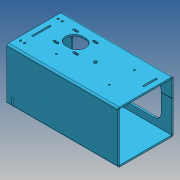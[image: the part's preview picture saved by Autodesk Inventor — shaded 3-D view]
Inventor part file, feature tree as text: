
AUTODESK INVENTOR PART (.ipt)
format: ipt  version: 2017 (Build 210142000, 142)  size: 420,352 bytes
history: native  units: mm
features: other x15, sketch x5, extrude x3, projected_geometry x1
ambient origin geometry x8: Origin, YZ Plane, XZ Plane, XY Plane, X Axis, Y Axis, Z Axis, Center Point
bodies: Body1 (feature_tree)
feature tree (24):
  other  "Sólido1"
  extrude  "Extrusión1"  Depth=56.4mm
  other  "Pestaña1"
  sketch  "Boceto4"  dims[d7=11.235mm]
  other  "Cara1"
  other  "Cara2"
  sketch  "Boceto5"  dims[d8=5.0mm d9=39.14mm d10=8.0mm d11=55.14mm d12=8.0mm d13=4.0mm d14=115.0mm d15=25.0mm d16=60.0mm d17=60.0mm d18=4.0mm d19=20.0mm d20=22.0mm d21=128.27mm d22=50.0mm d23=25.0mm d24=4.0mm d25=0.0mm d26=4.0mm d27=2.0mm d28=8.0mm d29=4.0mm d30=120.0mm d31=90.0deg d32=0.1mm d33=16.0mm d34=4.0mm d35=4.0mm d36=4.0mm d37=8.0mm d38=25.0mm d39=25.0mm d40=4.0mm d41=0.0mm d42=47.14mm d43=47.14mm d44=20.0mm d45=8.0mm d46=8.0mm d47=15.0mm d48=0.1mm d49=4.0mm d50=2.0mm d51=8.0mm d52=4.0mm d53=0.1mm d54=4.0mm d55=2.0mm d56=8.0mm d57=4.0mm d58=0.5mm d59=0.5mm d60=20.0mm d61=20.0mm d62=4.0mm d63=41.0mm d64=12.5mm d65=5.0mm d66=10.0mm d67=7.0mm d68=45.0mm d69=12.5mm d70=4.0mm d71=25.0mm d72=25.0mm d73=0.1mm d74=4.0mm d75=2.0mm d76=8.0mm d77=4.0mm d78=4.0mm d79=41.0mm d80=39.833333mm d81=79.666667mm d82=84.0mm d83=5.0mm d84=20.0mm d85=0.0mm]
  other  "Cara3"
  extrude  "Extrusión3"  Depth=67.5mm
  extrude  "Extrusión2"  Depth=8.0mm
  sketch  "Boceto1"  dims[d0=6.35mm d1=56.4mm]
  sketch  "Boceto2"  dims[d2=67.5mm d4=200.0mm]
  other  "Placa1"
  other  "Doblez1"
  other  "Esquina1"
  sketch  "Boceto3"  dims[d5=42.0mm d6=8.0mm]
  projected_geometry  "Contorno proyectado1"
  other  "Placa2"
  other  "Doblez2"
  other  "Placa3"
  other  "Doblez3"
  other  "Placa4"
  other  "Doblez4"
  other  "Definición1"
